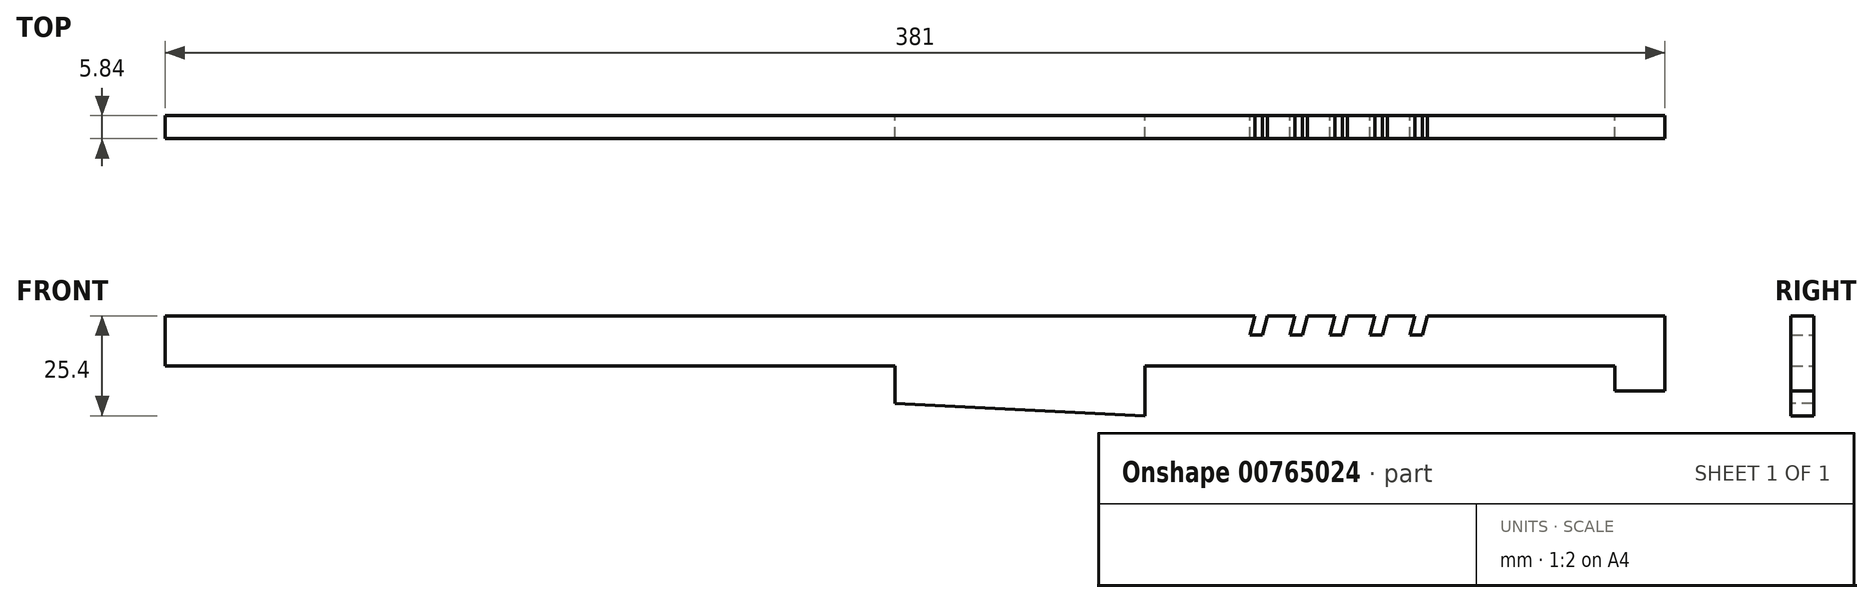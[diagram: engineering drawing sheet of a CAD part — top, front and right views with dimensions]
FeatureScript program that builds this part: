
annotation { "Feature Type Name" : "Feature", "Feature Type Description" : "" }
export const myFeature = defineFeature(function(context is Context, id is Id, definition is map)
    precondition{}
    {
        {
            var Q0;
            Q0=qCreatedBy(makeId("Front.planeOp"),FACE);
            var sketch = newSketch(context, id + "F0", { "sketchPlane" : qUnion([Q0])});
            skLineSegment(sketch, "E0.bottom", {"start": v(-190.5, 6.35) * mm, "end": v(86.36, 6.35) * mm});
            skLineSegment(sketch, "E0.top", {"start": v(-190.5, -6.35) * mm, "end": v(-5.08, -6.35) * mm});
            skLineSegment(sketch, "E0.left", {"start": v(-190.5, 6.35) * mm, "end": v(-190.5, -6.35) * mm});
            skLineSegment(sketch, "E0.right", {"start": v(190.5, 6.35) * mm, "end": v(190.5, -6.35) * mm});
            skPoint(sketch, "E0.middle", {"position": v(0, 0) * mm});
            skLineSegment(sketch, "E1", {"start": v(190.5, -6.35) * mm, "end": v(190.5, -12.7) * mm});
            skLineSegment(sketch, "E2", {"start": v(190.5, -12.7) * mm, "end": v(177.8, -12.7) * mm});
            skLineSegment(sketch, "E3", {"start": v(177.8, -12.7) * mm, "end": v(177.8, -6.35) * mm});
            skLineSegment(sketch, "E4", {"start": v(130.18, 6.35) * mm, "end": v(128.86, 1.44) * mm});
            skLineSegment(sketch, "E5", {"start": v(125.69, 1.44) * mm, "end": v(128.86, 1.44) * mm});
            skLineSegment(sketch, "E6", {"start": v(125.69, 1.44) * mm, "end": v(127, 6.35) * mm});
            skLineSegment(sketch, "E7.1.0.0", {"start": v(120.02, 6.35) * mm, "end": v(118.7, 1.44) * mm});
            skLineSegment(sketch, "E7.1.0.1", {"start": v(115.53, 1.44) * mm, "end": v(116.84, 6.35) * mm});
            skLineSegment(sketch, "E7.1.0.2", {"start": v(115.53, 1.44) * mm, "end": v(118.7, 1.44) * mm});
            skLineSegment(sketch, "E7.2.0.0", {"start": v(109.86, 6.35) * mm, "end": v(108.54, 1.44) * mm});
            skLineSegment(sketch, "E7.2.0.1", {"start": v(105.37, 1.44) * mm, "end": v(106.68, 6.35) * mm});
            skLineSegment(sketch, "E7.2.0.2", {"start": v(105.37, 1.44) * mm, "end": v(108.54, 1.44) * mm});
            skLineSegment(sketch, "E7.3.0.0", {"start": v(99.7, 6.35) * mm, "end": v(98.38, 1.44) * mm});
            skLineSegment(sketch, "E7.3.0.1", {"start": v(95.2, 1.44) * mm, "end": v(96.52, 6.35) * mm});
            skLineSegment(sketch, "E7.3.0.2", {"start": v(95.2, 1.44) * mm, "end": v(98.38, 1.44) * mm});
            skLineSegment(sketch, "E7.4.0.0", {"start": v(89.54, 6.35) * mm, "end": v(88.22, 1.44) * mm});
            skLineSegment(sketch, "E7.4.0.1", {"start": v(85.05, 1.44) * mm, "end": v(86.36, 6.35) * mm});
            skLineSegment(sketch, "E7.4.0.2", {"start": v(85.05, 1.44) * mm, "end": v(88.22, 1.44) * mm});
            skLineSegment(sketch, "E7.direction1", {"start": v(128.86, 1.44) * mm, "end": v(118.7, 1.44) * mm, "construction": true});
            skLineSegment(sketch, "E8.trimOffspring", {"start": v(89.53, 6.35) * mm, "end": v(96.52, 6.35) * mm});
            skLineSegment(sketch, "E9.trimOffspring", {"start": v(99.7, 6.35) * mm, "end": v(106.68, 6.35) * mm});
            skLineSegment(sketch, "E10.trimOffspring", {"start": v(109.86, 6.35) * mm, "end": v(116.84, 6.35) * mm});
            skLineSegment(sketch, "E11.trimOffspring", {"start": v(120.02, 6.35) * mm, "end": v(127, 6.35) * mm});
            skLineSegment(sketch, "E12.trimOffspring", {"start": v(130.18, 6.35) * mm, "end": v(190.5, 6.35) * mm});
            skLineSegment(sketch, "E13.top", {"start": v(-5.08, -19.05) * mm, "end": v(58.42, -19.05) * mm});
            skLineSegment(sketch, "E13.left", {"start": v(-5.08, -6.35) * mm, "end": v(-5.08, -19.05) * mm});
            skLineSegment(sketch, "E13.right", {"start": v(58.42, -6.35) * mm, "end": v(58.42, -19.05) * mm});
            skLineSegment(sketch, "E14.trimOffspring", {"start": v(58.42, -6.35) * mm, "end": v(177.8, -6.35) * mm});
            skSolve(sketch);
        }
        {
            var Q0;
            Q0 = qSketchRegion(id + "F0", true);
            extrude(context, id + "F1", {"entities" : qUnion([Q0]), "depth" : 5.84 * mm, "offsetDistance" : 25.4 * mm});
        }
        {
            var Q0;
            Q0=makeQuery(id+"F1.opExtrude","CAP_FACE",FACE,{"disambiguationData":[OSD([sQuery(id+"F0.wireOp",EDGE,"E0.bottom"),sQuery(id+"F0.wireOp",EDGE,"E0.top"),sQuery(id+"F0.wireOp",EDGE,"E0.left"),sQuery(id+"F0.wireOp",EDGE,"E0.right"),sQuery(id+"F0.wireOp",EDGE,"E1"),sQuery(id+"F0.wireOp",EDGE,"E2"),sQuery(id+"F0.wireOp",EDGE,"E3"),sQuery(id+"F0.wireOp",EDGE,"E4"),sQuery(id+"F0.wireOp",EDGE,"E5"),sQuery(id+"F0.wireOp",EDGE,"E6"),sQuery(id+"F0.wireOp",EDGE,"E7.1.0.0"),sQuery(id+"F0.wireOp",EDGE,"E7.1.0.1"),sQuery(id+"F0.wireOp",EDGE,"E7.1.0.2"),sQuery(id+"F0.wireOp",EDGE,"E7.2.0.0"),sQuery(id+"F0.wireOp",EDGE,"E7.2.0.1"),sQuery(id+"F0.wireOp",EDGE,"E7.2.0.2"),sQuery(id+"F0.wireOp",EDGE,"E7.3.0.0"),sQuery(id+"F0.wireOp",EDGE,"E7.3.0.1"),sQuery(id+"F0.wireOp",EDGE,"E7.3.0.2"),sQuery(id+"F0.wireOp",EDGE,"E7.4.0.0"),sQuery(id+"F0.wireOp",EDGE,"E7.4.0.1"),sQuery(id+"F0.wireOp",EDGE,"E7.4.0.2"),sQuery(id+"F0.wireOp",EDGE,"E8.trimOffspring"),sQuery(id+"F0.wireOp",EDGE,"E9.trimOffspring"),sQuery(id+"F0.wireOp",EDGE,"E10.trimOffspring"),sQuery(id+"F0.wireOp",EDGE,"E11.trimOffspring"),sQuery(id+"F0.wireOp",EDGE,"E12.trimOffspring"),sQuery(id+"F0.wireOp",EDGE,"E13.top"),sQuery(id+"F0.wireOp",EDGE,"E13.left"),sQuery(id+"F0.wireOp",EDGE,"E13.right"),sQuery(id+"F0.wireOp",EDGE,"E14.trimOffspring")])],"isStart":false});
            var sketch = newSketch(context, id + "F2", { "sketchPlane" : qUnion([Q0])});
            skLineSegment(sketch, "E15", {"start": v(-5.08, -15.87) * mm, "end": v(58.42, -19.05) * mm});
            skLineSegment(sketch, "E16", {"start": v(58.42, -19.05) * mm, "end": v(-5.08, -19.05) * mm});
            skLineSegment(sketch, "E17", {"start": v(-5.08, -19.05) * mm, "end": v(-5.08, -15.87) * mm});
            skSolve(sketch);
        }
        {
            var Q0;
            Q0 = qSketchRegion(id + "F2", true);
            extrude(context, id + "F3", {"entities" : qUnion([Q0]), "operationType" : NewBodyOperationType.REMOVE, "oppositeDirection" : true, "depth" : 25.4 * mm, "offsetDistance" : 25.4 * mm});
        }
    });
